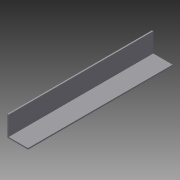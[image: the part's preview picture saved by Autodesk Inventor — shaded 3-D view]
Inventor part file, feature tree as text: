
AUTODESK INVENTOR PART (.ipt)
format: ipt  version: 2015 (Build 190159000, 159)  size: 90,112 bytes
history: native  units: in
note: dims shown in document units (in); Inventor stores cm internally (conversion verified against a paired STEP export)
features: extrude x4, sketch x4
ambient origin geometry x8: Origin, YZ Plane, XZ Plane, XY Plane, X Axis, Y Axis, Z Axis, Center Point
bodies: Solid1 (feature_tree)
feature tree (8):
  extrude  "Extrusion1"  Depth=0.125in
  extrude  "Extrusion2"  Depth=0.125in
  extrude  "Extrusion3"  Depth=14.0in TaperAngle=0.0deg
  extrude  "Extrusion4"  Depth=0.5in TaperAngle=0.0deg
  sketch  "Sketch1"  dims[d0=1.5in d1=0.125in]
  sketch  "Sketch2"  dims[d2=14.0in d3=0.0in d4=0.125in]
  sketch  "Sketch3"  dims[d5=1.5in d6=14.0in d7=0.0in]
  sketch  "Sketch4"  dims[d8=0.5in d9=0.0in d10=0.5in d11=0.0in]
